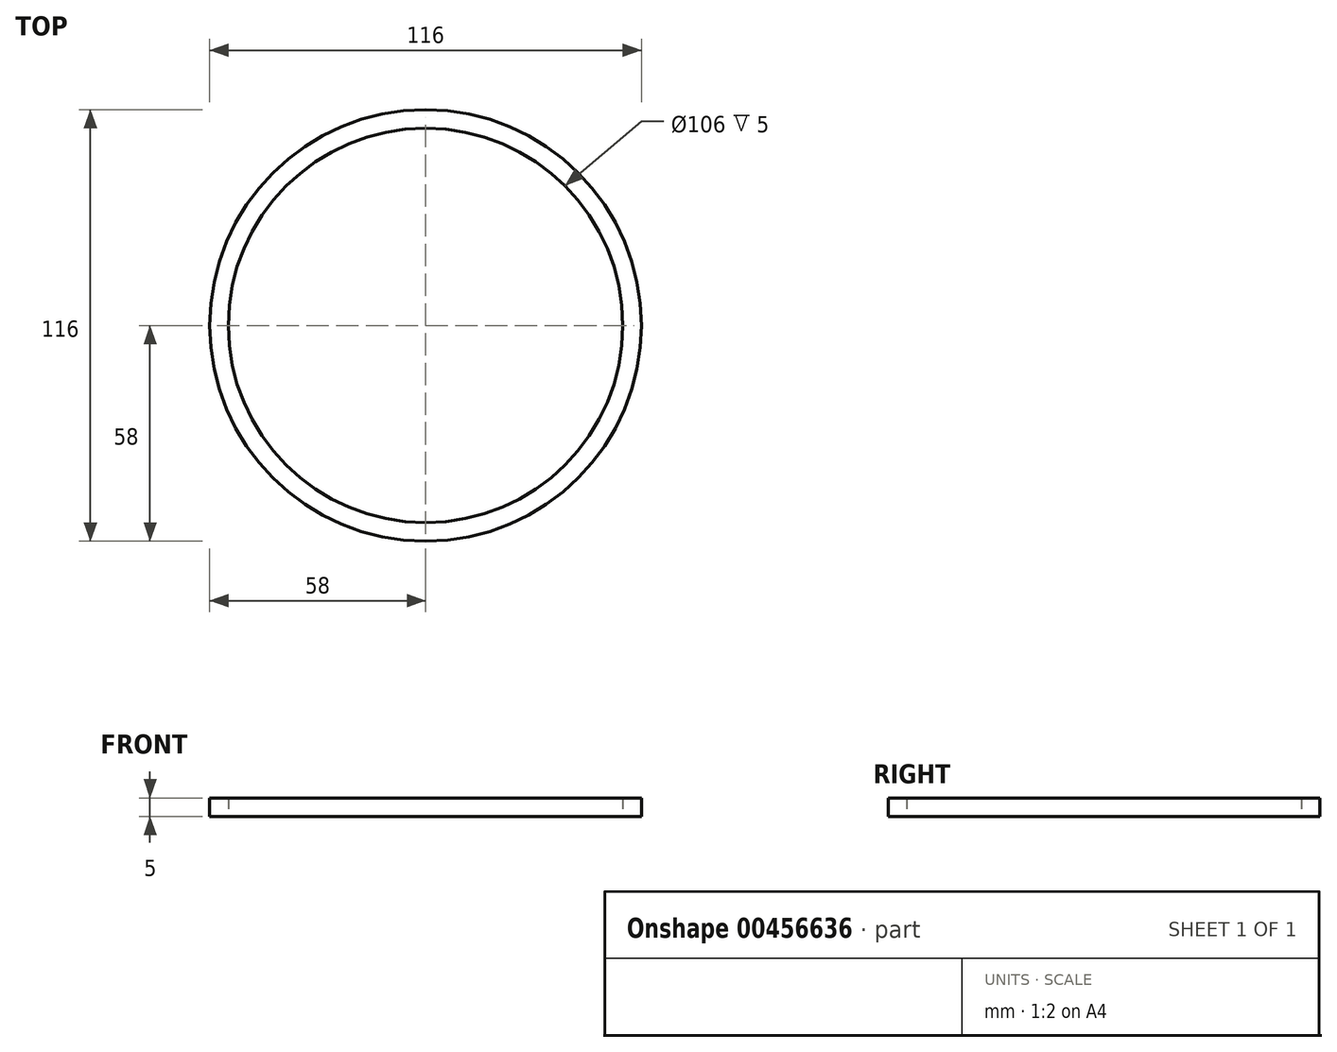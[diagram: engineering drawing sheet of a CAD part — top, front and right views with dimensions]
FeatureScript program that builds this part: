
annotation { "Feature Type Name" : "Feature", "Feature Type Description" : "" }
export const myFeature = defineFeature(function(context is Context, id is Id, definition is map)
    precondition{}
    {
        {
            var Q0;
            Q0=qCreatedBy(makeId("Top.planeOp"),FACE);
            var sketch = newSketch(context, id + "F0", { "sketchPlane" : qUnion([Q0])});
            skCircle(sketch, "E0", {"center": v(0, 0) * mm, "radius": 53 * mm});
            skCircle(sketch, "E1.0", {"center": v(0, 0) * mm, "radius": 58 * mm});
            skSolve(sketch);
        }
        {
            var Q0;
            Q0=makeQuery(id+"F0.imprint","IMPRINT",FACE,{"disambiguationData":[TD([[makeQuery(id+"F0.imprint","IMPRINT",EDGE,{"derivedFrom":sQuery(id+"F0.wireOp",EDGE,"E0")}),-1.0]])]});
            extrude(context, id + "F1", {"entities" : qUnion([Q0]), "depth" : 5 * mm});
        }
    });
